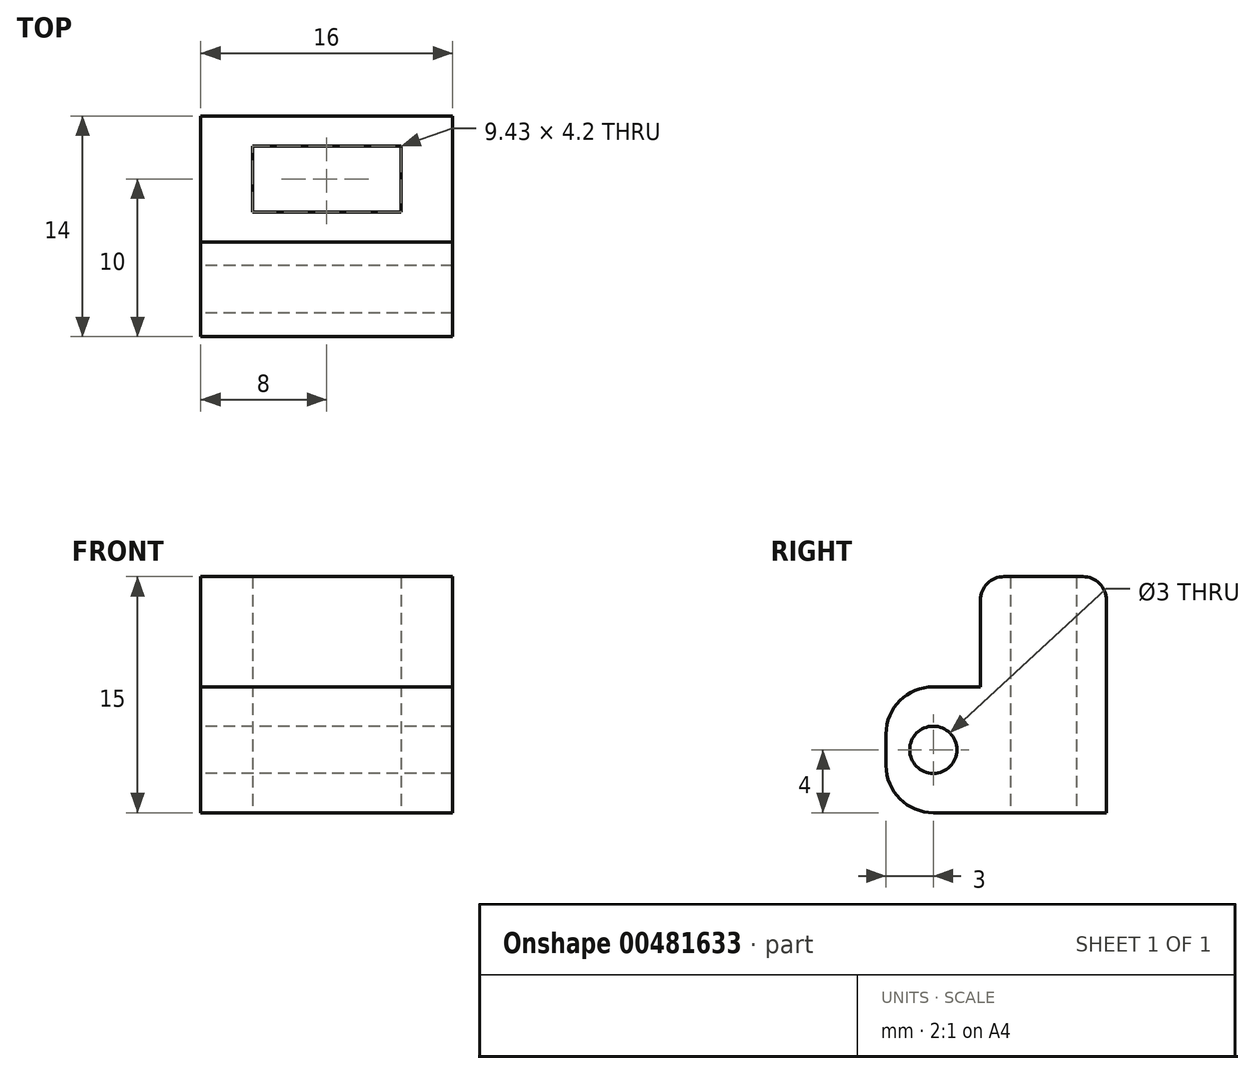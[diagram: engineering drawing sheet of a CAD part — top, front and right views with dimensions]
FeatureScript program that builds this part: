
annotation { "Feature Type Name" : "Feature", "Feature Type Description" : "" }
export const myFeature = defineFeature(function(context is Context, id is Id, definition is map)
    precondition{}
    {
        {
            var Q0;
            Q0=qCreatedBy(makeId("Top.planeOp"),FACE);
            var sketch = newSketch(context, id + "F0", { "sketchPlane" : qUnion([Q0])});
            skLineSegment(sketch, "E0.bottom", {"start": v(4.71, 2.1) * mm, "end": v(-4.71, 2.1) * mm});
            skLineSegment(sketch, "E0.top", {"start": v(4.71, -2.1) * mm, "end": v(-4.71, -2.1) * mm});
            skLineSegment(sketch, "E0.left", {"start": v(4.71, 2.1) * mm, "end": v(4.71, -2.1) * mm});
            skLineSegment(sketch, "E0.right", {"start": v(-4.71, 2.1) * mm, "end": v(-4.71, -2.1) * mm});
            skPoint(sketch, "E0.middle", {"position": v(0, 0) * mm});
            skLineSegment(sketch, "E1.bottom", {"start": v(8, 4) * mm, "end": v(-8, 4) * mm});
            skLineSegment(sketch, "E1.top", {"start": v(8, -4) * mm, "end": v(-8, -4) * mm});
            skLineSegment(sketch, "E1.left", {"start": v(8, 4) * mm, "end": v(8, -4) * mm});
            skLineSegment(sketch, "E1.right", {"start": v(-8, 4) * mm, "end": v(-8, -4) * mm});
            skSolve(sketch);
        }
        {
            var Q0;
            Q0 = qSketchRegion(id + "F0", true);
            extrude(context, id + "F1", {"entities" : qUnion([Q0]), "depth" : 15 * mm});
        }
        {
            var Q0;
            Q0=makeQuery(id+"F1.opExtrude","SWEPT_FACE",FACE,{"disambiguationData":[OSD([sQuery(id+"F0.wireOp",EDGE,"E1.top")])]});
            var sketch = newSketch(context, id + "F2", { "sketchPlane" : qUnion([Q0])});
            skLineSegment(sketch, "E2.bottom", {"start": v(-8, 0) * mm, "end": v(8, 0) * mm});
            skLineSegment(sketch, "E2.top", {"start": v(-8, 8) * mm, "end": v(8, 8) * mm});
            skLineSegment(sketch, "E2.left", {"start": v(-8, 0) * mm, "end": v(-8, 8) * mm});
            skLineSegment(sketch, "E2.right", {"start": v(8, 0) * mm, "end": v(8, 8) * mm});
            skSolve(sketch);
        }
        {
            var Q0;
            Q0=makeQuery(id+"F2.imprint","IMPRINT",FACE,{"disambiguationData":[TD([[makeQuery(id+"F2.imprint","IMPRINT",EDGE,{"derivedFrom":sQuery(id+"F2.wireOp",EDGE,"E2.bottom")}),-1.0]])]});
            extrude(context, id + "F3", {"entities" : qUnion([Q0]), "operationType" : NewBodyOperationType.ADD, "depth" : 6 * mm});
        }
        {
            var Q0;
            Q0=makeQuery(id+"F3.opExtrude","CAP_EDGE",EDGE,{"disambiguationData":[OSD([sQuery(id+"F2.wireOp",EDGE,"E2.bottom")])],"isStart":false});
            var Q1;
            Q1=makeQuery(id+"F3.opExtrude","CAP_EDGE",EDGE,{"disambiguationData":[OSD([sQuery(id+"F2.wireOp",EDGE,"E2.top")])],"isStart":false});
            fillet(context, id + "F4", {"entities" : qUnion([Q0, Q1]), "radius" : 3 * mm, "tangentPropagation" : true, "allowEdgeOverflow" : false});
        }
        {
            var Q0;
            Q0=makeQuery(id+"F3.boolean.opBoolean","MERGE",FACE,{"derivedFrom":[makeQuery(id+"F1.opExtrude","SWEPT_FACE",FACE,{"disambiguationData":[OSD([sQuery(id+"F0.wireOp",EDGE,"E1.right")])]}),makeQuery(id+"F3.opExtrude","SWEPT_FACE",FACE,{"disambiguationData":[OSD([sQuery(id+"F2.wireOp",EDGE,"E2.left")])]})]});
            var sketch = newSketch(context, id + "F5", { "sketchPlane" : qUnion([Q0])});
            skLineSegment(sketch, "E3", {"start": v(7, 8) * mm, "end": v(7, 0) * mm});
            skPoint(sketch, "E4", {"position": v(7, 4) * mm});
            skSolve(sketch);
        }
        {
            var Q0;
            Q0=sQuery(id+"F5.wireOp",VERTEX,"E4");
            var Q1;
            Q1=makeQuery(id+"F1.opExtrude","SWEPT_BODY",BODY,{"disambiguationData":[OSD([sQuery(id+"F0.wireOp",EDGE,"E0.bottom"),sQuery(id+"F0.wireOp",EDGE,"E0.top"),sQuery(id+"F0.wireOp",EDGE,"E0.left"),sQuery(id+"F0.wireOp",EDGE,"E0.right"),sQuery(id+"F0.wireOp",EDGE,"E1.bottom"),sQuery(id+"F0.wireOp",EDGE,"E1.top"),sQuery(id+"F0.wireOp",EDGE,"E1.left"),sQuery(id+"F0.wireOp",EDGE,"E1.right")])]});
            hole(context, id + "F6", {"style" : HoleStyle.SIMPLE, "endStyle" : HoleEndStyle.THROUGH, "holeDiameter" : 3 * mm, "isTappedThrough" : true, "tappedDepth" : 12 * mm, "tapClearance" : 3, "startFromSketch" : true, "locations" : qUnion([Q0]), "scope" : qUnion([Q1])});
        }
        {
            var Q0;
            Q0=makeQuery(id+"F1.opExtrude","CAP_EDGE",EDGE,{"disambiguationData":[OSD([sQuery(id+"F0.wireOp",EDGE,"E1.top")])],"isStart":false});
            var Q1;
            Q1=makeQuery(id+"F1.opExtrude","CAP_EDGE",EDGE,{"disambiguationData":[OSD([sQuery(id+"F0.wireOp",EDGE,"E1.bottom")])],"isStart":false});
            fillet(context, id + "F7", {"entities" : qUnion([Q0, Q1]), "radius" : 1.5 * mm, "tangentPropagation" : true, "allowEdgeOverflow" : false});
        }
    });
